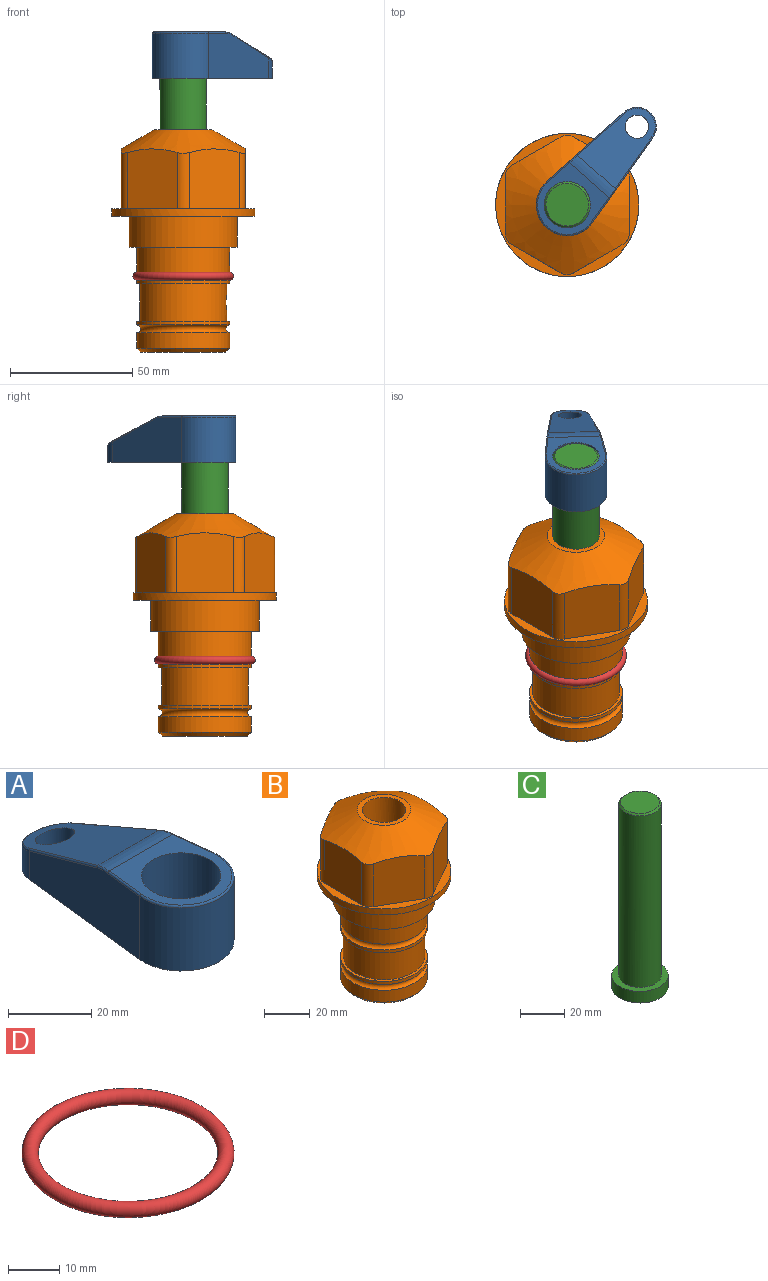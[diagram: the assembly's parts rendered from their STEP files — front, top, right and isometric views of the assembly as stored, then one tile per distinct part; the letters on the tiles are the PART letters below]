
ASSEMBLY  parts=4 mates=2
PART A: 44 faces, bbox 27.5x64.5x19.1 mm
  f0: plane 2.3x0.95mm, normal (0,0,-1), area 1mm2, adj f25,f30,f34
  f1: plane 63.5x25.4mm, normal (0,0,-1), area 561.7mm2, adj f2,f3,f4,f5,f6,f7,f19,f20
  f2: cylinder r=12.7mm len=25.4mm, axis (0,0,-1), area 792.2mm2, adj f1,f3,f5,f13
  f3: plane 42.33x18.54mm, normal (0.99,0.11,0), area 647mm2, adj f1,f2,f4,f11,f12,f14
  f4: cylinder r=7.94mm len=15.78mm, axis (0,0,-1), area 158.6mm2, adj f1,f3,f5,f16
  f5: plane 42.33x18.54mm, normal (-0.99,0.11,0), area 647mm2, adj f1,f2,f4,f15,f17,f18
  f6: cylinder r=9.53mm len=19.05mm, axis (0,0,-1), area 1140.1mm2, adj f1,f8
  f7: cylinder r=4.76mm len=10.98mm, axis (0,0,-1), area 276.1mm2, adj f1,f9
  f8: plane 25.83x24.38mm, normal (0,0,1), area 262.2mm2, adj f6,f10,f11,f13,f15
  f9: plane 32.49x20.55mm, normal (0,0.34,0.94), area 489.9mm2, adj f7,f10,f14,f16,f18
  f10: cylinder r=12.7mm len=21.49mm, axis (-1,0,0), area 93.2mm2, adj f8,f9,f12,f17
  f11: cylinder r=0.51mm len=12.34mm, axis (0.11,-0.99,0), area 9.9mm2, adj f3,f8,f12,f13
  f12: bspline ~7.62x1.64mm, area 3.5mm2, adj f3,f10,f11,f14
  f13: torus R=12.19mm, axis (0,0,1), area 33.6mm2, adj f2,f8,f11,f15
  f14: cylinder r=0.51mm len=26.01mm, axis (0.1,-0.93,0.34), area 21.6mm2, adj f3,f9,f12,f16
  f15: cylinder r=0.51mm len=12.34mm, axis (0.11,0.99,0), area 9.9mm2, adj f5,f8,f13,f17
  f16: bspline ~15.78x7.05mm, area 15.7mm2, adj f4,f9,f14,f18
  f17: bspline ~7.62x1.64mm, area 3.5mm2, adj f5,f10,f15,f18
  f18: cylinder r=0.51mm len=26.01mm, axis (0.1,0.93,-0.34), area 21.6mm2, adj f5,f9,f16,f17
  f19: plane 21.6x14.29mm, normal (-0.99,-0.11,0), area 242.6mm2, adj f1,f26,f28,f34,f36,f38
  f20: plane 21.6x14.29mm, normal (0.99,-0.11,0), area 242.6mm2, adj f1,f27,f29,f37,f39,f41
  f21: cylinder r=12.7mm len=14.29mm, axis (0,0,-1), area 173.2mm2, adj f1,f26,f27,f30,f31,f33
  f22: cylinder r=7.94mm len=7.63mm, axis (0,0,-1), area 53.8mm2, adj f1,f28,f29,f42
  f23: plane 2.3x0.95mm, normal (0,0,-1), area 1mm2, adj f25,f33,f37
  f24: plane 17.94x12.32mm, normal (0,-0.34,-0.94), area 191.2mm2, adj f25,f38,f41,f42
  f25: cylinder r=9.53mm len=12.93mm, axis (-1,0,0), area 37.5mm2, adj f0,f23,f24,f31,f36,f39
  f26: cylinder r=1.59mm len=14.29mm, axis (0,0,-1), area 49mm2, adj f1,f19,f21,f32
  f27: cylinder r=1.59mm len=14.29mm, axis (0,0,-1), area 49mm2, adj f1,f20,f21,f35
  f28: cylinder r=1.59mm len=7.28mm, axis (0,0,-1), area 22.1mm2, adj f1,f19,f22,f40
  f29: cylinder r=1.59mm len=7.28mm, axis (0,0,-1), area 22.1mm2, adj f1,f20,f22,f43
  f30: torus R=14.29mm, axis (0,0,1), area 5.8mm2, adj f0,f21,f31,f32
  f31: bspline ~11.06x2.73mm, area 20.8mm2, adj f21,f25,f30,f33
  f32: sphere r=1.59mm, area 5.4mm2, adj f26,f30,f34
  f33: torus R=14.29mm, axis (0,0,1), area 5.8mm2, adj f21,f23,f31,f35
  f34: cylinder r=1.59mm len=1.68mm, axis (-0.11,0.99,0), area 2.4mm2, adj f0,f19,f32,f36
  f35: sphere r=1.59mm, area 5.4mm2, adj f27,f33,f37
  f36: bspline ~5.82x2.33mm, area 7.7mm2, adj f19,f25,f34,f38
  f37: cylinder r=1.59mm len=1.68mm, axis (0.11,0.99,0), area 2.4mm2, adj f20,f23,f35,f39
  f38: cylinder r=1.59mm len=18.33mm, axis (0.1,-0.93,0.34), area 46.7mm2, adj f19,f24,f36,f40
  f39: bspline ~5.82x2.33mm, area 7.7mm2, adj f20,f25,f37,f41
  f40: sphere r=1.59mm, area 3.6mm2, adj f28,f38,f42
  f41: cylinder r=1.59mm len=18.33mm, axis (0.1,0.93,-0.34), area 46.7mm2, adj f20,f24,f39,f43
  f42: bspline ~8.31x1.84mm, area 15.3mm2, adj f22,f24,f40,f43
  f43: sphere r=1.59mm, area 3.6mm2, adj f29,f41,f42
PART B: 36 faces, bbox 58.7x58.7x91.2 mm
  f0: cylinder r=17.78mm len=35.56mm, axis (0,0,1), area 1670.8mm2, adj f23,f24,f31
  f1: cylinder r=19.05mm len=38.1mm, axis (0,0,1), area 1191.9mm2, adj f26,f27,f30
  f2: plane 58.66x58.66mm, normal (0,0,-1), area 1150.6mm2, adj f3,f28
  f3: cylinder r=29.33mm len=58.66mm, axis (0,0,-1), area 585.1mm2, adj f2,f4
  f4: plane 58.66x58.66mm, normal (0,0,1), area 475.9mm2, adj f3,f5,f6,f7,f8,f9,f10,f11
  f5: plane 24.5x20.32mm, normal (-0.5,0.87,0), area 562.8mm2, adj f4,f15,f16,f17
  f6: plane 24.5x20.32mm, normal (0.5,0.87,0), area 562.8mm2, adj f4,f14,f15,f17
  f7: plane 24.5x23.48mm, normal (1,0,0), area 562.8mm2, adj f4,f13,f14,f17
  f8: plane 24.5x20.32mm, normal (0.5,-0.87,0), area 562.8mm2, adj f4,f12,f13,f17
  f9: plane 24.5x20.32mm, normal (-0.5,-0.87,0), area 562.8mm2, adj f4,f11,f12,f17
  f10: plane 24.5x23.48mm, normal (-1,0,0), area 562.8mm2, adj f4,f11,f16,f17
  f11: cylinder r=5.08mm len=23.01mm, axis (0,0,-1), area 121.2mm2, adj f4,f9,f10,f17
  f12: cylinder r=5.08mm len=23.01mm, axis (0,0,-1), area 121.2mm2, adj f4,f8,f9,f17
  f13: cylinder r=5.08mm len=23.01mm, axis (0,0,-1), area 121.2mm2, adj f4,f7,f8,f17
  f14: cylinder r=5.08mm len=23.01mm, axis (0,0,-1), area 121.2mm2, adj f4,f6,f7,f17
  f15: cylinder r=5.08mm len=23.01mm, axis (0,0,-1), area 121.2mm2, adj f4,f5,f6,f17
  f16: cylinder r=5.08mm len=23.01mm, axis (0,0,-1), area 121.2mm2, adj f4,f5,f10,f17
  f17: cone r=11.73mm half-angle=60deg, axis (0,0,-1), area 2071.8mm2, adj f5,f6,f7,f8,f9,f10,f11,f12
  f18: plane 23.46x23.46mm, normal (0,0,1), area 147.4mm2, adj f17,f35
  f19: plane 34.93x34.93mm, normal (0,0,-1), area 958mm2, adj f29
  f20: cylinder r=19.05mm len=38.1mm, axis (0,0,1), area 760.1mm2, adj f21,f29
  f21: torus R=19.05mm, axis (0,0,1), area 565.3mm2, adj f20,f22
  f22: cylinder r=19.05mm len=38.1mm, axis (0,0,1), area 190mm2, adj f21,f23
  f23: plane 38.1x38.1mm, normal (0,0,1), area 146.9mm2, adj f0,f22
  f24: plane 38.1x38.1mm, normal (0,0,-1), area 146.9mm2, adj f0,f25
  f25: cylinder r=19.05mm len=38.1mm, axis (0,0,1), area 190mm2, adj f24,f26
  f26: torus R=19.05mm, axis (0,0,1), area 565.3mm2, adj f1,f25
  f27: plane 44.45x44.45mm, normal (0,0,-1), area 411.7mm2, adj f1,f28
  f28: cylinder r=22.23mm len=44.45mm, axis (0,0,1), area 1773.5mm2, adj f2,f27
  f29: cone r=19.05mm half-angle=45deg, axis (0,0,1), area 257.5mm2, adj f19,f20
  f30: cylinder r=3.17mm len=6.75mm, axis (-1,0,0), area 128mm2, adj f1,f33
  f31: cylinder r=3.17mm len=6.35mm, axis (-1,0,0), area 102.5mm2, adj f0,f33
  f32: plane 25.4x25.4mm, normal (0,0,1), area 506.7mm2, adj f33
  f33: cylinder r=12.7mm len=66.42mm, axis (0,0,-1), area 5236.2mm2, adj f30,f31,f32,f34
  f34: cone r=9.53mm half-angle=30deg, axis (0,0,-1), area 443.4mm2, adj f33,f35
  f35: cylinder r=9.53mm len=19.05mm, axis (0,0,-1), area 849mm2, adj f18,f34
PART C: 6 faces, bbox 25.4x25.4x101.6 mm
  f0: plane 17.46x17.46mm, normal (0,0,1), area 239.5mm2, adj f5
  f1: plane 25.4x25.4mm, normal (0,0,-1), area 506.7mm2, adj f2
  f2: cylinder r=12.7mm len=25.4mm, axis (0,0,1), area 506.7mm2, adj f1,f3
  f3: plane 25.4x25.4mm, normal (0,0,1), area 221.7mm2, adj f2,f4
  f4: cylinder r=9.53mm len=94.46mm, axis (0,0,1), area 5653mm2, adj f3,f5
  f5: cone r=8.73mm half-angle=45deg, axis (0,0,-1), area 64.4mm2, adj f0,f4
PART D: 1 faces, bbox 44.7x44.7x3.2 mm
  f0: torus R=19.05mm, axis (0,0,1), area 1193.9mm2
PLACE A rot(axis=(0,0,-1),41.8deg) t=(0,0,56.53)mm fixed
PLACE B at identity fixed
PLACE C rot(axis=(0,0,-1),41.8deg) t=(0,0,1.92)mm
PLACE D at identity
MATE fastened A.f2 <-> C.f2  axis (0,0,-1) through (0,0,75.58)mm
MATE cylindrical C.f2 <-> B.f0  axis (0,0,1) through (0,0,27.56)mm
